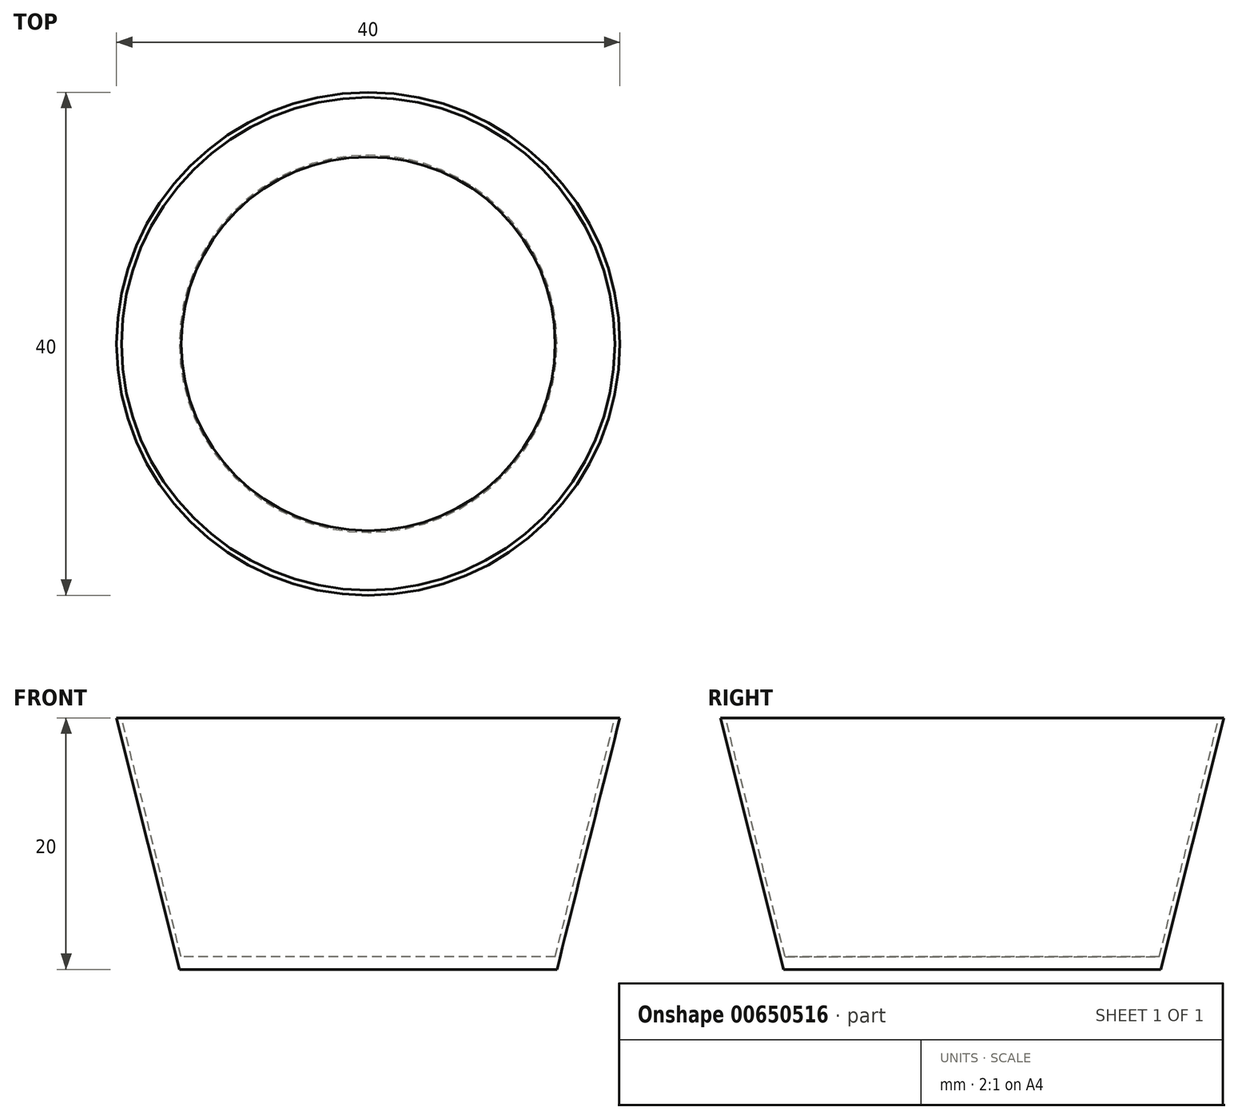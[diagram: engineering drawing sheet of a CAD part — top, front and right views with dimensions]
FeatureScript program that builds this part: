
annotation { "Feature Type Name" : "Feature", "Feature Type Description" : "" }
export const myFeature = defineFeature(function(context is Context, id is Id, definition is map)
    precondition{}
    {
        {
            var Q0;
            Q0=qCreatedBy(makeId("Top.planeOp"),FACE);
            var sketch = newSketch(context, id + "F0", { "sketchPlane" : qUnion([Q0])});
            skCircle(sketch, "E0", {"center": v(0, 0) * mm, "radius": 20 * mm});
            skSolve(sketch);
        }
        {
            var Q0;
            Q0 = qSketchRegion(id + "F0", true);
            extrude(context, id + "F1", {"entities" : qUnion([Q0]), "depth" : 20 * mm, "offsetDistance" : 25 * mm});
        }
        {
            var Q0;
            Q0=makeQuery(id+"F1.opExtrude","CAP_EDGE",EDGE,{"disambiguationData":[OSD([sQuery(id+"F0.wireOp",EDGE,"E0")])],"isStart":true});
            chamfer(context, id + "F2", {"entities" : qUnion([Q0]), "chamferType" : ChamferType.TWO_OFFSETS, "width1" : 20 * mm, "oppositeDirection" : false, "width2" : 5 * mm, "tangentPropagation" : true});
        }
        {
            var Q0;
            Q0=makeQuery(id+"F1.opExtrude","CAP_FACE",FACE,{"disambiguationData":[OSD([sQuery(id+"F0.wireOp",EDGE,"E0")])],"isStart":false});
            var sketch = newSketch(context, id + "F3", { "sketchPlane" : qUnion([Q0])});
            skCircle(sketch, "E1", {"center": v(0, 0) * mm, "radius": 19.6 * mm});
            skSolve(sketch);
        }
        {
            var Q0;
            Q0=makeQuery(id+"F3.imprint","IMPRINT",FACE,{"disambiguationData":[TD([[makeQuery(id+"F3.imprint","IMPRINT",EDGE,{"derivedFrom":sQuery(id+"F3.wireOp",EDGE,"E1")}),1.0]])]});
            extrude(context, id + "F4", {"entities" : qUnion([Q0]), "operationType" : NewBodyOperationType.REMOVE, "oppositeDirection" : true, "depth" : 19 * mm, "offsetDistance" : 25 * mm, "hasDraft" : true, "draftAngle" : 14 * degree, "draftPullDirection" : true});
        }
    });
